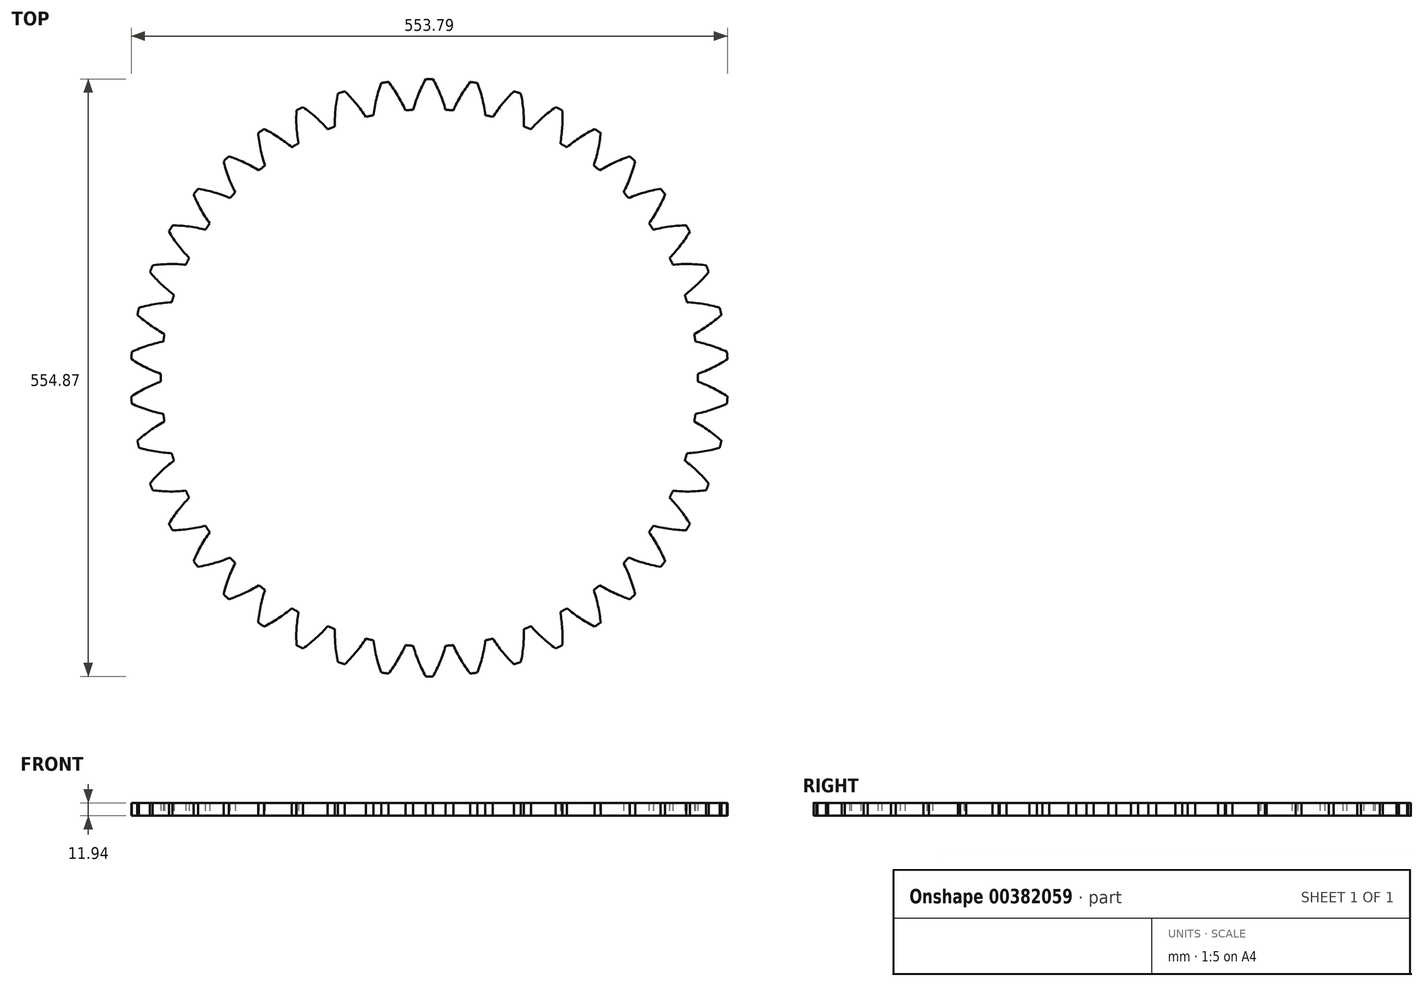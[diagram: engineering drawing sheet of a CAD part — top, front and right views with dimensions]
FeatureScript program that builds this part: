
annotation { "Feature Type Name" : "Feature", "Feature Type Description" : "" }
export const myFeature = defineFeature(function(context is Context, id is Id, definition is map)
    precondition{}
    {
        {
            var Q0;
            Q0=qCreatedBy(makeId("Top.planeOp"),FACE);
            var sketch = newSketch(context, id + "F0", { "sketchPlane" : qUnion([Q0])});
            skArc(sketch, "E0.0", {"start": v(-54.32, -94.08) * mm, "mid": v(-94.58, 56.19) * mm, "end": v(55.68, 96.45) * mm});
            skArc(sketch, "E0.1", {"start": v(55.68, 96.45) * mm, "mid": v(95.95, -53.81) * mm, "end": v(-54.32, -94.08) * mm});
            skArc(sketch, "E1.0", {"start": v(-29.98, 96.5) * mm, "mid": v(-28.83, 96.86) * mm, "end": v(-27.67, 97.21) * mm});
            skArc(sketch, "E1.1", {"start": v(-29.98, 96.5) * mm, "mid": v(-30.81, 91) * mm, "end": v(-30.99, 85.43) * mm});
            skArc(sketch, "E1.2", {"start": v(-30.99, 85.43) * mm, "mid": v(-32.2, 84.96) * mm, "end": v(-33.4, 84.48) * mm});
            skArc(sketch, "E1.3", {"start": v(-33.4, 84.48) * mm, "mid": v(-37.31, 88.44) * mm, "end": v(-41.66, 91.91) * mm});
            skArc(sketch, "E1.4", {"start": v(-43.85, 90.86) * mm, "mid": v(-42.76, 91.4) * mm, "end": v(-41.66, 91.91) * mm});
            skArc(sketch, "E1.5", {"start": v(-43.85, 90.86) * mm, "mid": v(-43.85, 85.3) * mm, "end": v(-43.2, 79.77) * mm});
            skArc(sketch, "E1.6", {"start": v(-43.2, 79.77) * mm, "mid": v(-44.32, 79.13) * mm, "end": v(-45.43, 78.47) * mm});
            skArc(sketch, "E1.7", {"start": v(-45.43, 78.47) * mm, "mid": v(-49.9, 81.8) * mm, "end": v(-54.71, 84.59) * mm});
            skArc(sketch, "E1.8", {"start": v(-54.71, 84.59) * mm, "mid": v(-55.72, 83.91) * mm, "end": v(-56.71, 83.23) * mm});
            skArc(sketch, "E1.9", {"start": v(-56.71, 83.23) * mm, "mid": v(-55.88, 77.72) * mm, "end": v(-54.41, 72.35) * mm});
            skArc(sketch, "E1.10", {"start": v(-54.41, 72.35) * mm, "mid": v(-55.43, 71.55) * mm, "end": v(-56.43, 70.74) * mm});
            skArc(sketch, "E1.11", {"start": v(-56.43, 70.74) * mm, "mid": v(-61.34, 73.37) * mm, "end": v(-66.53, 75.4) * mm});
            skArc(sketch, "E2.0", {"start": v(-66.53, 75.4) * mm, "mid": v(-67.42, 74.58) * mm, "end": v(-68.3, 73.75) * mm});
            skArc(sketch, "E2.1", {"start": v(-68.3, 73.75) * mm, "mid": v(-66.66, 68.43) * mm, "end": v(-64.4, 63.34) * mm});
            skArc(sketch, "E2.2", {"start": v(-64.4, 63.34) * mm, "mid": v(-65.3, 62.4) * mm, "end": v(-66.16, 61.45) * mm});
            skArc(sketch, "E2.3", {"start": v(-66.16, 61.45) * mm, "mid": v(-71.4, 63.32) * mm, "end": v(-76.84, 64.55) * mm});
            skArc(sketch, "E2.4", {"start": v(-76.84, 64.55) * mm, "mid": v(-77.6, 63.61) * mm, "end": v(-78.35, 62.66) * mm});
            skArc(sketch, "E2.5", {"start": v(-78.35, 62.66) * mm, "mid": v(-75.93, 57.65) * mm, "end": v(-72.94, 52.95) * mm});
            skArc(sketch, "E2.6", {"start": v(-72.94, 52.95) * mm, "mid": v(-73.68, 51.88) * mm, "end": v(-74.4, 50.81) * mm});
            skArc(sketch, "E2.7", {"start": v(-74.4, 50.81) * mm, "mid": v(-79.86, 51.88) * mm, "end": v(-85.42, 52.3) * mm});
            skArc(sketch, "E2.8", {"start": v(-86.63, 50.2) * mm, "mid": v(-86.03, 51.25) * mm, "end": v(-85.42, 52.3) * mm});
            skArc(sketch, "E2.9", {"start": v(-86.63, 50.2) * mm, "mid": v(-83.49, 45.6) * mm, "end": v(-79.83, 41.4) * mm});
            skArc(sketch, "E2.10", {"start": v(-79.83, 41.4) * mm, "mid": v(-80.4, 40.24) * mm, "end": v(-80.96, 39.07) * mm});
            skArc(sketch, "E2.11", {"start": v(-80.96, 39.07) * mm, "mid": v(-86.52, 39.3) * mm, "end": v(-92.07, 38.89) * mm});
            skArc(sketch, "E2.12", {"start": v(-92.07, 38.89) * mm, "mid": v(-92.52, 37.77) * mm, "end": v(-92.96, 36.64) * mm});
            skArc(sketch, "E2.13", {"start": v(-84.93, 28.95) * mm, "mid": v(-89.17, 32.55) * mm, "end": v(-92.96, 36.64) * mm});
            skArc(sketch, "E2.14", {"start": v(-85.69, 26.48) * mm, "mid": v(-85.32, 27.71) * mm, "end": v(-84.93, 28.95) * mm});
            skArc(sketch, "E2.15", {"start": v(-85.69, 26.48) * mm, "mid": v(-91.23, 25.88) * mm, "end": v(-96.65, 24.64) * mm});
            skArc(sketch, "E2.16", {"start": v(-96.65, 24.64) * mm, "mid": v(-96.93, 23.47) * mm, "end": v(-97.2, 22.28) * mm});
            skArc(sketch, "E3.0", {"start": v(-97.2, 22.28) * mm, "mid": v(-93.36, 19.19) * mm, "end": v(-89.23, 16.5) * mm});
            skArc(sketch, "E3.1", {"start": v(-88.5, 13.32) * mm, "mid": v(-88.31, 14.6) * mm, "end": v(-88.1, 15.88) * mm});
            skArc(sketch, "E3.2", {"start": v(-88.5, 13.32) * mm, "mid": v(-93.88, 11.9) * mm, "end": v(-99.06, 9.87) * mm});
            skArc(sketch, "E3.3", {"start": v(-88.1, 15.88) * mm, "mid": v(-88.67, 16.19) * mm, "end": v(-89.23, 16.5) * mm});
            skArc(sketch, "E3.4", {"start": v(-99.24, 7.46) * mm, "mid": v(-99.16, 8.67) * mm, "end": v(-99.06, 9.87) * mm});
            skArc(sketch, "E3.5", {"start": v(-99.24, 7.46) * mm, "mid": v(-98.07, 6.71) * mm, "end": v(-96.87, 6) * mm});
            skArc(sketch, "E3.6", {"start": v(-89.3, 2.48) * mm, "mid": v(-93.17, 4.07) * mm, "end": v(-96.87, 6) * mm});
            skArc(sketch, "E3.7", {"start": v(-89.3, -0.1) * mm, "mid": v(-89.32, 1.19) * mm, "end": v(-89.3, 2.48) * mm});
            skArc(sketch, "E3.8", {"start": v(-89.3, -0.1) * mm, "mid": v(-94.42, -2.3) * mm, "end": v(-99.24, -5.09) * mm});
            skArc(sketch, "E3.9", {"start": v(-99.24, -5.09) * mm, "mid": v(-99.16, -6.3) * mm, "end": v(-99.06, -7.5) * mm});
            skArc(sketch, "E3.10", {"start": v(-99.06, -7.5) * mm, "mid": v(-93.88, -9.54) * mm, "end": v(-88.5, -10.95) * mm});
            skArc(sketch, "E3.11", {"start": v(-88.5, -10.95) * mm, "mid": v(-88.31, -12.23) * mm, "end": v(-88.1, -13.5) * mm});
            skArc(sketch, "E3.12", {"start": v(-88.1, -13.5) * mm, "mid": v(-92.84, -16.44) * mm, "end": v(-97.2, -19.91) * mm});
            skArc(sketch, "E3.13", {"start": v(-97.2, -19.91) * mm, "mid": v(-96.93, -21.1) * mm, "end": v(-96.65, -22.27) * mm});
            skArc(sketch, "E3.14", {"start": v(-96.65, -22.27) * mm, "mid": v(-91.23, -23.51) * mm, "end": v(-85.69, -24.1) * mm});
            skArc(sketch, "E3.15", {"start": v(-85.69, -24.1) * mm, "mid": v(-85.32, -25.34) * mm, "end": v(-84.93, -26.57) * mm});
            skArc(sketch, "E3.16", {"start": v(-84.93, -26.57) * mm, "mid": v(-89.17, -30.18) * mm, "end": v(-92.96, -34.27) * mm});
            skArc(sketch, "E3.17", {"start": v(-92.07, -36.52) * mm, "mid": v(-92.52, -35.4) * mm, "end": v(-92.96, -34.27) * mm});
            skArc(sketch, "E3.18", {"start": v(-92.07, -36.52) * mm, "mid": v(-86.52, -36.93) * mm, "end": v(-80.95, -36.7) * mm});
            skArc(sketch, "E3.19", {"start": v(-80.95, -36.7) * mm, "mid": v(-80.4, -37.86) * mm, "end": v(-79.83, -39.02) * mm});
            skArc(sketch, "E3.20", {"start": v(-79.83, -39.02) * mm, "mid": v(-83.49, -43.22) * mm, "end": v(-86.63, -47.83) * mm});
            skArc(sketch, "E3.21", {"start": v(-86.63, -47.83) * mm, "mid": v(-86.03, -48.88) * mm, "end": v(-85.42, -49.92) * mm});
            skArc(sketch, "E3.22", {"start": v(-85.42, -49.92) * mm, "mid": v(-79.86, -49.5) * mm, "end": v(-74.4, -48.44) * mm});
            skArc(sketch, "E3.23", {"start": v(-74.4, -48.44) * mm, "mid": v(-73.68, -49.51) * mm, "end": v(-72.94, -50.58) * mm});
            skArc(sketch, "E3.24", {"start": v(-78.35, -60.3) * mm, "mid": v(-75.93, -55.27) * mm, "end": v(-72.94, -50.58) * mm});
            skArc(sketch, "E3.25", {"start": v(-78.35, -60.3) * mm, "mid": v(-77.6, -61.24) * mm, "end": v(-76.84, -62.18) * mm});
            skArc(sketch, "E3.26", {"start": v(-76.84, -62.18) * mm, "mid": v(-71.4, -60.94) * mm, "end": v(-66.16, -59.08) * mm});
            skArc(sketch, "E3.27", {"start": v(-66.16, -59.08) * mm, "mid": v(-65.29, -60.03) * mm, "end": v(-64.4, -60.97) * mm});
            skArc(sketch, "E3.28", {"start": v(-64.4, -60.97) * mm, "mid": v(-66.66, -66.06) * mm, "end": v(-68.3, -71.38) * mm});
            skArc(sketch, "E3.29", {"start": v(-68.3, -71.38) * mm, "mid": v(-67.42, -72.21) * mm, "end": v(-66.53, -73.03) * mm});
            skArc(sketch, "E3.30", {"start": v(-56.43, -68.37) * mm, "mid": v(-61.34, -71) * mm, "end": v(-66.53, -73.03) * mm});
            skArc(sketch, "E3.31", {"start": v(-56.43, -68.37) * mm, "mid": v(-55.43, -69.18) * mm, "end": v(-54.41, -69.98) * mm});
            skArc(sketch, "E3.32", {"start": v(-54.41, -69.98) * mm, "mid": v(-55.88, -75.35) * mm, "end": v(-56.71, -80.85) * mm});
            skArc(sketch, "E4.0", {"start": v(-54.71, -82.22) * mm, "mid": v(-55.72, -81.54) * mm, "end": v(-56.71, -80.85) * mm});
            skArc(sketch, "E5.0", {"start": v(-54.71, -82.22) * mm, "mid": v(-49.9, -79.43) * mm, "end": v(-45.43, -76.1) * mm});
            skArc(sketch, "E6.0", {"start": v(-44.32, -76.76) * mm, "mid": v(-44.87, -76.43) * mm, "end": v(-45.43, -76.1) * mm});
            skArc(sketch, "E7.0", {"start": v(-43.2, -77.4) * mm, "mid": v(-43.75, -77.08) * mm, "end": v(-44.32, -76.76) * mm});
            skArc(sketch, "E8.0", {"start": v(-43.2, -77.4) * mm, "mid": v(-43.85, -82.92) * mm, "end": v(-43.85, -88.5) * mm});
            skArc(sketch, "E9.0", {"start": v(-41.66, -89.54) * mm, "mid": v(-42.76, -89.02) * mm, "end": v(-43.85, -88.5) * mm});
            skArc(sketch, "E10.0", {"start": v(-41.66, -89.54) * mm, "mid": v(-37.31, -86.07) * mm, "end": v(-33.4, -82.11) * mm});
            skArc(sketch, "E11.0", {"start": v(-33.4, -82.11) * mm, "mid": v(-32.2, -82.6) * mm, "end": v(-30.99, -83.06) * mm});
            skArc(sketch, "E12.0", {"start": v(-30.99, -83.06) * mm, "mid": v(-30.81, -88.62) * mm, "end": v(-29.98, -94.13) * mm});
            skArc(sketch, "E13.0", {"start": v(-29.98, -94.13) * mm, "mid": v(-28.83, -94.5) * mm, "end": v(-27.67, -94.84) * mm});
            skArc(sketch, "E14.0", {"start": v(-27.67, -94.84) * mm, "mid": v(-23.88, -90.76) * mm, "end": v(-20.6, -86.26) * mm});
            skArc(sketch, "E15.0", {"start": v(-20.6, -86.26) * mm, "mid": v(-19.34, -86.56) * mm, "end": v(-18.08, -86.84) * mm});
            skArc(sketch, "E16.0", {"start": v(-18.08, -86.84) * mm, "mid": v(-17.08, -92.31) * mm, "end": v(-15.43, -97.63) * mm});
            skArc(sketch, "E17.0", {"start": v(-15.43, -97.63) * mm, "mid": v(-14.24, -97.82) * mm, "end": v(-13.04, -98) * mm});
            skArc(sketch, "E18.0", {"start": v(-7.33, -88.46) * mm, "mid": v(-9.9, -93.4) * mm, "end": v(-13.04, -98) * mm});
            skArc(sketch, "E19.0", {"start": v(-4.75, -88.65) * mm, "mid": v(-6.04, -88.56) * mm, "end": v(-7.33, -88.46) * mm});
            skArc(sketch, "E20.0", {"start": v(-4.75, -88.65) * mm, "mid": v(-2.94, -93.92) * mm, "end": v(-0.53, -98.93) * mm});
            skArc(sketch, "E21.0", {"start": v(-0.53, -98.93) * mm, "mid": v(0.68, -98.94) * mm, "end": v(1.9, -98.93) * mm});
            skArc(sketch, "E22.0", {"start": v(1.9, -98.93) * mm, "mid": v(4.31, -93.92) * mm, "end": v(6.12, -88.65) * mm});
            skArc(sketch, "E23.0", {"start": v(8.7, -88.46) * mm, "mid": v(7.41, -88.56) * mm, "end": v(6.12, -88.65) * mm});
            skArc(sketch, "E24.0", {"start": v(14.4, -98) * mm, "mid": v(11.27, -93.4) * mm, "end": v(8.7, -88.46) * mm});
            skArc(sketch, "E25.0", {"start": v(16.8, -97.63) * mm, "mid": v(15.6, -97.82) * mm, "end": v(14.4, -98) * mm});
            skArc(sketch, "E26.0", {"start": v(16.8, -97.63) * mm, "mid": v(18.45, -92.31) * mm, "end": v(19.45, -86.84) * mm});
            skArc(sketch, "E27.0", {"start": v(19.45, -86.84) * mm, "mid": v(20.71, -86.56) * mm, "end": v(21.97, -86.26) * mm});
            skArc(sketch, "E28.0", {"start": v(21.97, -86.26) * mm, "mid": v(25.25, -90.76) * mm, "end": v(29.04, -94.84) * mm});
            skArc(sketch, "E29.0", {"start": v(29.04, -94.84) * mm, "mid": v(30.2, -94.5) * mm, "end": v(31.35, -94.13) * mm});
            skArc(sketch, "E30.0", {"start": v(32.36, -83.06) * mm, "mid": v(32.18, -88.62) * mm, "end": v(31.35, -94.13) * mm});
            skArc(sketch, "E31.0", {"start": v(34.77, -82.11) * mm, "mid": v(33.57, -82.6) * mm, "end": v(32.36, -83.06) * mm});
            skArc(sketch, "E32.0", {"start": v(34.77, -82.11) * mm, "mid": v(38.68, -86.07) * mm, "end": v(43.03, -89.54) * mm});
            skArc(sketch, "E33.0", {"start": v(43.03, -89.54) * mm, "mid": v(44.13, -89.02) * mm, "end": v(45.22, -88.5) * mm});
            skArc(sketch, "E34.0", {"start": v(45.22, -88.5) * mm, "mid": v(45.22, -82.92) * mm, "end": v(44.56, -77.4) * mm});
            skArc(sketch, "E35.0", {"start": v(46.8, -76.1) * mm, "mid": v(45.68, -76.76) * mm, "end": v(44.56, -77.4) * mm});
            skArc(sketch, "E36.0", {"start": v(46.8, -76.1) * mm, "mid": v(50.1, -78.65) * mm, "end": v(53.63, -80.9) * mm});
            skArc(sketch, "E37.0", {"start": v(53.63, -80.9) * mm, "mid": v(54.85, -81.57) * mm, "end": v(56.08, -82.22) * mm});
            skArc(sketch, "E38.0", {"start": v(58.08, -80.85) * mm, "mid": v(57.09, -81.54) * mm, "end": v(56.08, -82.22) * mm});
            skArc(sketch, "E39.0", {"start": v(55.78, -69.98) * mm, "mid": v(57.25, -75.35) * mm, "end": v(58.08, -80.85) * mm});
            skArc(sketch, "E40.0", {"start": v(57.8, -68.37) * mm, "mid": v(56.8, -69.18) * mm, "end": v(55.78, -69.98) * mm});
            skArc(sketch, "E41.0", {"start": v(67.9, -73.03) * mm, "mid": v(63.3, -71.26) * mm, "end": v(58.9, -69.02) * mm});
            skArc(sketch, "E42.0", {"start": v(58.9, -69.02) * mm, "mid": v(58.35, -68.7) * mm, "end": v(57.8, -68.37) * mm});
            skArc(sketch, "E43.0", {"start": v(67.9, -73.03) * mm, "mid": v(68.79, -72.21) * mm, "end": v(69.67, -71.38) * mm});
            skArc(sketch, "E44.0", {"start": v(69.67, -71.38) * mm, "mid": v(68.03, -66.06) * mm, "end": v(65.77, -60.97) * mm});
            skArc(sketch, "E45.0", {"start": v(67.53, -59.08) * mm, "mid": v(66.66, -60.03) * mm, "end": v(65.77, -60.97) * mm});
            skArc(sketch, "E46.0", {"start": v(67.53, -59.08) * mm, "mid": v(72.78, -60.94) * mm, "end": v(78.2, -62.18) * mm});
            skArc(sketch, "E47.0", {"start": v(78.2, -62.18) * mm, "mid": v(78.97, -61.24) * mm, "end": v(79.72, -60.3) * mm});
            skArc(sketch, "E48.0", {"start": v(74.31, -50.58) * mm, "mid": v(77.3, -55.27) * mm, "end": v(79.72, -60.3) * mm});
            skArc(sketch, "E49.0", {"start": v(75.77, -48.44) * mm, "mid": v(75.05, -49.51) * mm, "end": v(74.31, -50.58) * mm});
            skArc(sketch, "E50.0", {"start": v(75.77, -48.44) * mm, "mid": v(81.23, -49.5) * mm, "end": v(86.78, -49.92) * mm});
            skArc(sketch, "E51.0", {"start": v(88, -47.83) * mm, "mid": v(87.4, -48.88) * mm, "end": v(86.78, -49.92) * mm});
            skArc(sketch, "E52.0", {"start": v(81.2, -39.02) * mm, "mid": v(84.86, -43.22) * mm, "end": v(88, -47.83) * mm});
            skArc(sketch, "E53.0.0", {"start": v(55.68, 96.45) * mm, "mid": v(-94.58, 56.19) * mm, "end": v(-54.32, -94.08) * mm});
            skArc(sketch, "E53.0.1", {"start": v(-54.32, -94.08) * mm, "mid": v(95.95, -53.81) * mm, "end": v(55.68, 96.45) * mm});
            skArc(sketch, "E54.0", {"start": v(82.32, -36.7) * mm, "mid": v(81.77, -37.86) * mm, "end": v(81.2, -39.02) * mm});
            skArc(sketch, "E55.0", {"start": v(82.32, -36.7) * mm, "mid": v(87.89, -36.93) * mm, "end": v(93.44, -36.52) * mm});
            skArc(sketch, "E56.0", {"start": v(93.44, -36.52) * mm, "mid": v(93.89, -35.4) * mm, "end": v(94.32, -34.26) * mm});
            skArc(sketch, "E57.0", {"start": v(94.32, -34.26) * mm, "mid": v(90.54, -30.18) * mm, "end": v(86.3, -26.57) * mm});
            skArc(sketch, "E58.0", {"start": v(86.3, -26.57) * mm, "mid": v(86.69, -25.34) * mm, "end": v(87.06, -24.1) * mm});
            skArc(sketch, "E59.0", {"start": v(87.06, -24.1) * mm, "mid": v(92.6, -23.51) * mm, "end": v(98.02, -22.27) * mm});
            skArc(sketch, "E60.0", {"start": v(98.02, -22.27) * mm, "mid": v(98.3, -21.1) * mm, "end": v(98.56, -19.91) * mm});
            skArc(sketch, "E61.0", {"start": v(98.56, -19.91) * mm, "mid": v(94.2, -16.44) * mm, "end": v(89.48, -13.5) * mm});
            skArc(sketch, "E62.0", {"start": v(89.48, -13.5) * mm, "mid": v(89.68, -12.23) * mm, "end": v(89.86, -10.95) * mm});
            skArc(sketch, "E63.0", {"start": v(100.43, -7.5) * mm, "mid": v(95.25, -9.54) * mm, "end": v(89.86, -10.95) * mm});
            skArc(sketch, "E64.0", {"start": v(100.43, -7.5) * mm, "mid": v(100.53, -6.3) * mm, "end": v(100.61, -5.09) * mm});
            skArc(sketch, "E65.0", {"start": v(100.61, -5.09) * mm, "mid": v(95.8, -2.3) * mm, "end": v(90.68, -0.1) * mm});
            skArc(sketch, "E66.0", {"start": v(90.68, -0.1) * mm, "mid": v(90.68, 1.19) * mm, "end": v(90.68, 2.48) * mm});
            skArc(sketch, "E67.0", {"start": v(90.68, 2.48) * mm, "mid": v(95.8, 4.68) * mm, "end": v(100.61, 7.46) * mm});
            skArc(sketch, "E68.0", {"start": v(100.61, 7.46) * mm, "mid": v(100.53, 8.67) * mm, "end": v(100.43, 9.87) * mm});
            skArc(sketch, "E69.0", {"start": v(100.43, 9.87) * mm, "mid": v(95.25, 11.9) * mm, "end": v(89.86, 13.32) * mm});
            skArc(sketch, "E70.0", {"start": v(89.86, 13.32) * mm, "mid": v(89.68, 14.6) * mm, "end": v(89.48, 15.88) * mm});
            skArc(sketch, "E71.0", {"start": v(89.48, 15.88) * mm, "mid": v(94.2, 18.81) * mm, "end": v(98.56, 22.28) * mm});
            skArc(sketch, "E72.0", {"start": v(98.56, 22.28) * mm, "mid": v(98.3, 23.47) * mm, "end": v(98.02, 24.64) * mm});
            skArc(sketch, "E73.0", {"start": v(98.02, 24.64) * mm, "mid": v(92.6, 25.88) * mm, "end": v(87.06, 26.48) * mm});
            skArc(sketch, "E74.0", {"start": v(87.06, 26.48) * mm, "mid": v(86.69, 27.71) * mm, "end": v(86.3, 28.95) * mm});
            skArc(sketch, "E75.0", {"start": v(86.3, 28.95) * mm, "mid": v(90.54, 32.55) * mm, "end": v(94.32, 36.64) * mm});
            skArc(sketch, "E76.0", {"start": v(94.32, 36.64) * mm, "mid": v(93.89, 37.77) * mm, "end": v(93.44, 38.89) * mm});
            skArc(sketch, "E77.0", {"start": v(93.44, 38.89) * mm, "mid": v(87.89, 39.3) * mm, "end": v(82.32, 39.07) * mm});
            skArc(sketch, "E78.0", {"start": v(81.2, 41.4) * mm, "mid": v(81.77, 40.24) * mm, "end": v(82.32, 39.07) * mm});
            skArc(sketch, "E79.0", {"start": v(81.2, 41.4) * mm, "mid": v(84.86, 45.6) * mm, "end": v(88, 50.2) * mm});
            skArc(sketch, "E80.0", {"start": v(88, 50.2) * mm, "mid": v(87.4, 51.25) * mm, "end": v(86.78, 52.3) * mm});
            skArc(sketch, "E81.0", {"start": v(75.77, 50.81) * mm, "mid": v(81.23, 51.88) * mm, "end": v(86.78, 52.3) * mm});
            skArc(sketch, "E82.0", {"start": v(75.77, 50.81) * mm, "mid": v(75.05, 51.88) * mm, "end": v(74.31, 52.95) * mm});
            skArc(sketch, "E83.0", {"start": v(79.72, 62.66) * mm, "mid": v(77.3, 57.65) * mm, "end": v(74.31, 52.95) * mm});
            skArc(sketch, "E84.0", {"start": v(79.72, 62.66) * mm, "mid": v(78.97, 63.61) * mm, "end": v(78.2, 64.56) * mm});
            skArc(sketch, "E85.0", {"start": v(78.2, 64.56) * mm, "mid": v(72.78, 63.32) * mm, "end": v(67.53, 61.45) * mm});
            skArc(sketch, "E86.0", {"start": v(65.77, 63.34) * mm, "mid": v(66.66, 62.4) * mm, "end": v(67.53, 61.45) * mm});
            skArc(sketch, "E87.0", {"start": v(69.67, 73.75) * mm, "mid": v(68.03, 68.43) * mm, "end": v(65.77, 63.34) * mm});
            skArc(sketch, "E88.0", {"start": v(69.67, 73.75) * mm, "mid": v(68.79, 74.58) * mm, "end": v(67.9, 75.4) * mm});
            skArc(sketch, "E89.0", {"start": v(67.9, 75.4) * mm, "mid": v(62.71, 73.37) * mm, "end": v(57.8, 70.74) * mm});
            skArc(sketch, "E90.0", {"start": v(57.8, 70.74) * mm, "mid": v(56.8, 71.55) * mm, "end": v(55.78, 72.35) * mm});
            skArc(sketch, "E91.0", {"start": v(55.78, 72.35) * mm, "mid": v(57.25, 77.72) * mm, "end": v(58.08, 83.23) * mm});
            skArc(sketch, "E92.0", {"start": v(58.08, 83.23) * mm, "mid": v(57.09, 83.91) * mm, "end": v(56.08, 84.59) * mm});
            skArc(sketch, "E93.0", {"start": v(56.08, 84.59) * mm, "mid": v(51.26, 81.8) * mm, "end": v(46.8, 78.47) * mm});
            skArc(sketch, "E94.0", {"start": v(44.56, 79.77) * mm, "mid": v(45.68, 79.13) * mm, "end": v(46.8, 78.47) * mm});
            skArc(sketch, "E95.0", {"start": v(44.56, 79.77) * mm, "mid": v(45.22, 85.3) * mm, "end": v(45.21, 90.86) * mm});
            skArc(sketch, "E96.0", {"start": v(45.21, 90.86) * mm, "mid": v(44.13, 91.4) * mm, "end": v(43.03, 91.91) * mm});
            skArc(sketch, "E97.0", {"start": v(43.03, 91.91) * mm, "mid": v(38.68, 88.44) * mm, "end": v(34.76, 84.48) * mm});
            skArc(sketch, "E98.0", {"start": v(34.76, 84.48) * mm, "mid": v(33.57, 84.96) * mm, "end": v(32.36, 85.43) * mm});
            skArc(sketch, "E99.0", {"start": v(32.36, 85.43) * mm, "mid": v(32.18, 91) * mm, "end": v(31.35, 96.5) * mm});
            skArc(sketch, "E100.0", {"start": v(31.35, 96.5) * mm, "mid": v(30.2, 96.86) * mm, "end": v(29.04, 97.21) * mm});
            skArc(sketch, "E101.0", {"start": v(29.04, 97.21) * mm, "mid": v(25.25, 93.13) * mm, "end": v(21.97, 88.63) * mm});
            skArc(sketch, "E102.0", {"start": v(19.45, 89.2) * mm, "mid": v(20.71, 88.93) * mm, "end": v(21.97, 88.63) * mm});
            skArc(sketch, "E103.0", {"start": v(19.45, 89.2) * mm, "mid": v(18.44, 94.68) * mm, "end": v(16.8, 100) * mm});
            skArc(sketch, "E104.0", {"start": v(16.8, 100) * mm, "mid": v(15.6, 100.2) * mm, "end": v(14.4, 100.37) * mm});
            skArc(sketch, "E105.0", {"start": v(8.7, 90.83) * mm, "mid": v(11.27, 95.77) * mm, "end": v(14.4, 100.37) * mm});
            skArc(sketch, "E106.0", {"start": v(8.7, 90.83) * mm, "mid": v(7.41, 90.93) * mm, "end": v(6.12, 91.02) * mm});
            skArc(sketch, "E107.0", {"start": v(6.12, 91.02) * mm, "mid": v(4.31, 96.29) * mm, "end": v(1.9, 101.3) * mm});
            skArc(sketch, "E108.0", {"start": v(1.9, 101.3) * mm, "mid": v(0.68, 101.31) * mm, "end": v(-0.53, 101.3) * mm});
            skArc(sketch, "E109.0", {"start": v(-0.53, 101.3) * mm, "mid": v(-2.94, 96.29) * mm, "end": v(-4.75, 91.02) * mm});
            skArc(sketch, "E110.0", {"start": v(-7.33, 90.83) * mm, "mid": v(-6.04, 90.93) * mm, "end": v(-4.75, 91.02) * mm});
            skArc(sketch, "E111.0", {"start": v(-20.6, 88.63) * mm, "mid": v(-23.88, 93.13) * mm, "end": v(-27.67, 97.21) * mm});
            skArc(sketch, "E112.0", {"start": v(-18.08, 89.2) * mm, "mid": v(-19.34, 88.93) * mm, "end": v(-20.6, 88.63) * mm});
            skArc(sketch, "E113.0", {"start": v(-15.43, 100) * mm, "mid": v(-17.08, 94.68) * mm, "end": v(-18.08, 89.2) * mm});
            skArc(sketch, "E114.0", {"start": v(-13.04, 100.37) * mm, "mid": v(-14.24, 100.2) * mm, "end": v(-15.43, 100) * mm});
            skArc(sketch, "E115.0", {"start": v(-7.33, 90.83) * mm, "mid": v(-9.9, 95.77) * mm, "end": v(-13.04, 100.37) * mm});
            skSolve(sketch);
        }
        {
            var Q0;
            Q0=makeQuery(id+"F0.imprint","IMPRINT",FACE,{"disambiguationData":[TD([[makeQuery(id+"F0.imprint","IMPRINT",EDGE,{"derivedFrom":sQuery(id+"F0.wireOp",EDGE,"E1.0")}),1.0]])]});
            extrude(context, id + "F1", {"entities" : qUnion([Q0]), "depth" : 4.3 * mm});
        }
        {
            var Q0;
            Q0=makeQuery(id+"F1.opExtrude","SWEPT_BODY",BODY,{"disambiguationData":[OSD([sQuery(id+"F0.wireOp",EDGE,"E1.0"),sQuery(id+"F0.wireOp",EDGE,"E1.1"),sQuery(id+"F0.wireOp",EDGE,"E1.2"),sQuery(id+"F0.wireOp",EDGE,"E1.3"),sQuery(id+"F0.wireOp",EDGE,"E1.4"),sQuery(id+"F0.wireOp",EDGE,"E1.5"),sQuery(id+"F0.wireOp",EDGE,"E1.6"),sQuery(id+"F0.wireOp",EDGE,"E1.7"),sQuery(id+"F0.wireOp",EDGE,"E1.8"),sQuery(id+"F0.wireOp",EDGE,"E1.9"),sQuery(id+"F0.wireOp",EDGE,"E1.10"),sQuery(id+"F0.wireOp",EDGE,"E1.11"),sQuery(id+"F0.wireOp",EDGE,"E2.0"),sQuery(id+"F0.wireOp",EDGE,"E2.1"),sQuery(id+"F0.wireOp",EDGE,"E2.2"),sQuery(id+"F0.wireOp",EDGE,"E2.3"),sQuery(id+"F0.wireOp",EDGE,"E2.4"),sQuery(id+"F0.wireOp",EDGE,"E2.5"),sQuery(id+"F0.wireOp",EDGE,"E2.6"),sQuery(id+"F0.wireOp",EDGE,"E2.7"),sQuery(id+"F0.wireOp",EDGE,"E2.8"),sQuery(id+"F0.wireOp",EDGE,"E2.9"),sQuery(id+"F0.wireOp",EDGE,"E2.10"),sQuery(id+"F0.wireOp",EDGE,"E2.11"),sQuery(id+"F0.wireOp",EDGE,"E2.12"),sQuery(id+"F0.wireOp",EDGE,"E2.13"),sQuery(id+"F0.wireOp",EDGE,"E2.14"),sQuery(id+"F0.wireOp",EDGE,"E2.15"),sQuery(id+"F0.wireOp",EDGE,"E2.16"),sQuery(id+"F0.wireOp",EDGE,"E3.0"),sQuery(id+"F0.wireOp",EDGE,"E3.1"),sQuery(id+"F0.wireOp",EDGE,"E3.2"),sQuery(id+"F0.wireOp",EDGE,"E3.3"),sQuery(id+"F0.wireOp",EDGE,"E3.4"),sQuery(id+"F0.wireOp",EDGE,"E3.5"),sQuery(id+"F0.wireOp",EDGE,"E3.6"),sQuery(id+"F0.wireOp",EDGE,"E3.7"),sQuery(id+"F0.wireOp",EDGE,"E3.8"),sQuery(id+"F0.wireOp",EDGE,"E3.9"),sQuery(id+"F0.wireOp",EDGE,"E3.10"),sQuery(id+"F0.wireOp",EDGE,"E3.11"),sQuery(id+"F0.wireOp",EDGE,"E3.12"),sQuery(id+"F0.wireOp",EDGE,"E3.13"),sQuery(id+"F0.wireOp",EDGE,"E3.14"),sQuery(id+"F0.wireOp",EDGE,"E3.15"),sQuery(id+"F0.wireOp",EDGE,"E3.16"),sQuery(id+"F0.wireOp",EDGE,"E3.17"),sQuery(id+"F0.wireOp",EDGE,"E3.18"),sQuery(id+"F0.wireOp",EDGE,"E3.19"),sQuery(id+"F0.wireOp",EDGE,"E3.20"),sQuery(id+"F0.wireOp",EDGE,"E3.21"),sQuery(id+"F0.wireOp",EDGE,"E3.22"),sQuery(id+"F0.wireOp",EDGE,"E3.23"),sQuery(id+"F0.wireOp",EDGE,"E3.24"),sQuery(id+"F0.wireOp",EDGE,"E3.25"),sQuery(id+"F0.wireOp",EDGE,"E3.26"),sQuery(id+"F0.wireOp",EDGE,"E3.27"),sQuery(id+"F0.wireOp",EDGE,"E3.28"),sQuery(id+"F0.wireOp",EDGE,"E3.29"),sQuery(id+"F0.wireOp",EDGE,"E3.30"),sQuery(id+"F0.wireOp",EDGE,"E3.31"),sQuery(id+"F0.wireOp",EDGE,"E3.32"),sQuery(id+"F0.wireOp",EDGE,"E4.0"),sQuery(id+"F0.wireOp",EDGE,"E5.0"),sQuery(id+"F0.wireOp",EDGE,"E6.0"),sQuery(id+"F0.wireOp",EDGE,"E7.0"),sQuery(id+"F0.wireOp",EDGE,"E8.0"),sQuery(id+"F0.wireOp",EDGE,"E9.0"),sQuery(id+"F0.wireOp",EDGE,"E10.0"),sQuery(id+"F0.wireOp",EDGE,"E11.0"),sQuery(id+"F0.wireOp",EDGE,"E12.0"),sQuery(id+"F0.wireOp",EDGE,"E13.0"),sQuery(id+"F0.wireOp",EDGE,"E14.0"),sQuery(id+"F0.wireOp",EDGE,"E15.0"),sQuery(id+"F0.wireOp",EDGE,"E16.0"),sQuery(id+"F0.wireOp",EDGE,"E17.0"),sQuery(id+"F0.wireOp",EDGE,"E18.0"),sQuery(id+"F0.wireOp",EDGE,"E19.0"),sQuery(id+"F0.wireOp",EDGE,"E20.0"),sQuery(id+"F0.wireOp",EDGE,"E21.0"),sQuery(id+"F0.wireOp",EDGE,"E22.0"),sQuery(id+"F0.wireOp",EDGE,"E23.0"),sQuery(id+"F0.wireOp",EDGE,"E24.0"),sQuery(id+"F0.wireOp",EDGE,"E25.0"),sQuery(id+"F0.wireOp",EDGE,"E26.0"),sQuery(id+"F0.wireOp",EDGE,"E27.0"),sQuery(id+"F0.wireOp",EDGE,"E28.0"),sQuery(id+"F0.wireOp",EDGE,"E29.0"),sQuery(id+"F0.wireOp",EDGE,"E30.0"),sQuery(id+"F0.wireOp",EDGE,"E31.0"),sQuery(id+"F0.wireOp",EDGE,"E32.0"),sQuery(id+"F0.wireOp",EDGE,"E33.0"),sQuery(id+"F0.wireOp",EDGE,"E34.0"),sQuery(id+"F0.wireOp",EDGE,"E35.0"),sQuery(id+"F0.wireOp",EDGE,"E36.0"),sQuery(id+"F0.wireOp",EDGE,"E37.0"),sQuery(id+"F0.wireOp",EDGE,"E38.0"),sQuery(id+"F0.wireOp",EDGE,"E39.0"),sQuery(id+"F0.wireOp",EDGE,"E40.0"),sQuery(id+"F0.wireOp",EDGE,"E41.0"),sQuery(id+"F0.wireOp",EDGE,"E42.0"),sQuery(id+"F0.wireOp",EDGE,"E43.0"),sQuery(id+"F0.wireOp",EDGE,"E44.0"),sQuery(id+"F0.wireOp",EDGE,"E45.0"),sQuery(id+"F0.wireOp",EDGE,"E46.0"),sQuery(id+"F0.wireOp",EDGE,"E47.0"),sQuery(id+"F0.wireOp",EDGE,"E48.0"),sQuery(id+"F0.wireOp",EDGE,"E49.0"),sQuery(id+"F0.wireOp",EDGE,"E50.0"),sQuery(id+"F0.wireOp",EDGE,"E51.0"),sQuery(id+"F0.wireOp",EDGE,"E52.0"),sQuery(id+"F0.wireOp",EDGE,"E53.0.0"),sQuery(id+"F0.wireOp",EDGE,"E53.0.1"),sQuery(id+"F0.wireOp",EDGE,"E54.0"),sQuery(id+"F0.wireOp",EDGE,"E55.0"),sQuery(id+"F0.wireOp",EDGE,"E56.0"),sQuery(id+"F0.wireOp",EDGE,"E57.0"),sQuery(id+"F0.wireOp",EDGE,"E58.0"),sQuery(id+"F0.wireOp",EDGE,"E59.0"),sQuery(id+"F0.wireOp",EDGE,"E60.0"),sQuery(id+"F0.wireOp",EDGE,"E61.0"),sQuery(id+"F0.wireOp",EDGE,"E62.0"),sQuery(id+"F0.wireOp",EDGE,"E63.0"),sQuery(id+"F0.wireOp",EDGE,"E64.0"),sQuery(id+"F0.wireOp",EDGE,"E65.0"),sQuery(id+"F0.wireOp",EDGE,"E66.0"),sQuery(id+"F0.wireOp",EDGE,"E67.0"),sQuery(id+"F0.wireOp",EDGE,"E68.0"),sQuery(id+"F0.wireOp",EDGE,"E69.0"),sQuery(id+"F0.wireOp",EDGE,"E70.0"),sQuery(id+"F0.wireOp",EDGE,"E71.0"),sQuery(id+"F0.wireOp",EDGE,"E72.0"),sQuery(id+"F0.wireOp",EDGE,"E73.0"),sQuery(id+"F0.wireOp",EDGE,"E74.0"),sQuery(id+"F0.wireOp",EDGE,"E75.0"),sQuery(id+"F0.wireOp",EDGE,"E76.0"),sQuery(id+"F0.wireOp",EDGE,"E77.0"),sQuery(id+"F0.wireOp",EDGE,"E78.0"),sQuery(id+"F0.wireOp",EDGE,"E79.0"),sQuery(id+"F0.wireOp",EDGE,"E80.0"),sQuery(id+"F0.wireOp",EDGE,"E81.0"),sQuery(id+"F0.wireOp",EDGE,"E82.0"),sQuery(id+"F0.wireOp",EDGE,"E83.0"),sQuery(id+"F0.wireOp",EDGE,"E84.0"),sQuery(id+"F0.wireOp",EDGE,"E85.0"),sQuery(id+"F0.wireOp",EDGE,"E86.0"),sQuery(id+"F0.wireOp",EDGE,"E87.0"),sQuery(id+"F0.wireOp",EDGE,"E88.0"),sQuery(id+"F0.wireOp",EDGE,"E89.0"),sQuery(id+"F0.wireOp",EDGE,"E90.0"),sQuery(id+"F0.wireOp",EDGE,"E91.0"),sQuery(id+"F0.wireOp",EDGE,"E92.0"),sQuery(id+"F0.wireOp",EDGE,"E93.0"),sQuery(id+"F0.wireOp",EDGE,"E94.0"),sQuery(id+"F0.wireOp",EDGE,"E95.0"),sQuery(id+"F0.wireOp",EDGE,"E96.0"),sQuery(id+"F0.wireOp",EDGE,"E97.0"),sQuery(id+"F0.wireOp",EDGE,"E98.0"),sQuery(id+"F0.wireOp",EDGE,"E99.0"),sQuery(id+"F0.wireOp",EDGE,"E100.0"),sQuery(id+"F0.wireOp",EDGE,"E101.0"),sQuery(id+"F0.wireOp",EDGE,"E102.0"),sQuery(id+"F0.wireOp",EDGE,"E103.0"),sQuery(id+"F0.wireOp",EDGE,"E104.0"),sQuery(id+"F0.wireOp",EDGE,"E105.0"),sQuery(id+"F0.wireOp",EDGE,"E106.0"),sQuery(id+"F0.wireOp",EDGE,"E107.0"),sQuery(id+"F0.wireOp",EDGE,"E108.0"),sQuery(id+"F0.wireOp",EDGE,"E109.0"),sQuery(id+"F0.wireOp",EDGE,"E110.0"),sQuery(id+"F0.wireOp",EDGE,"E111.0"),sQuery(id+"F0.wireOp",EDGE,"E112.0"),sQuery(id+"F0.wireOp",EDGE,"E113.0"),sQuery(id+"F0.wireOp",EDGE,"E114.0"),sQuery(id+"F0.wireOp",EDGE,"E115.0")])]});
            var Q1;
            Q1=qCreatedBy(makeId("Origin.pointOp"),VERTEX);
            transform(context, id + "F2", {"entities" : qUnion([Q0]), "transformType" : TransformType.SCALE_UNIFORMLY, "scale" : 2.77, "scalePoint" : qUnion([Q1]), "makeCopy" : false});
        }
    });
